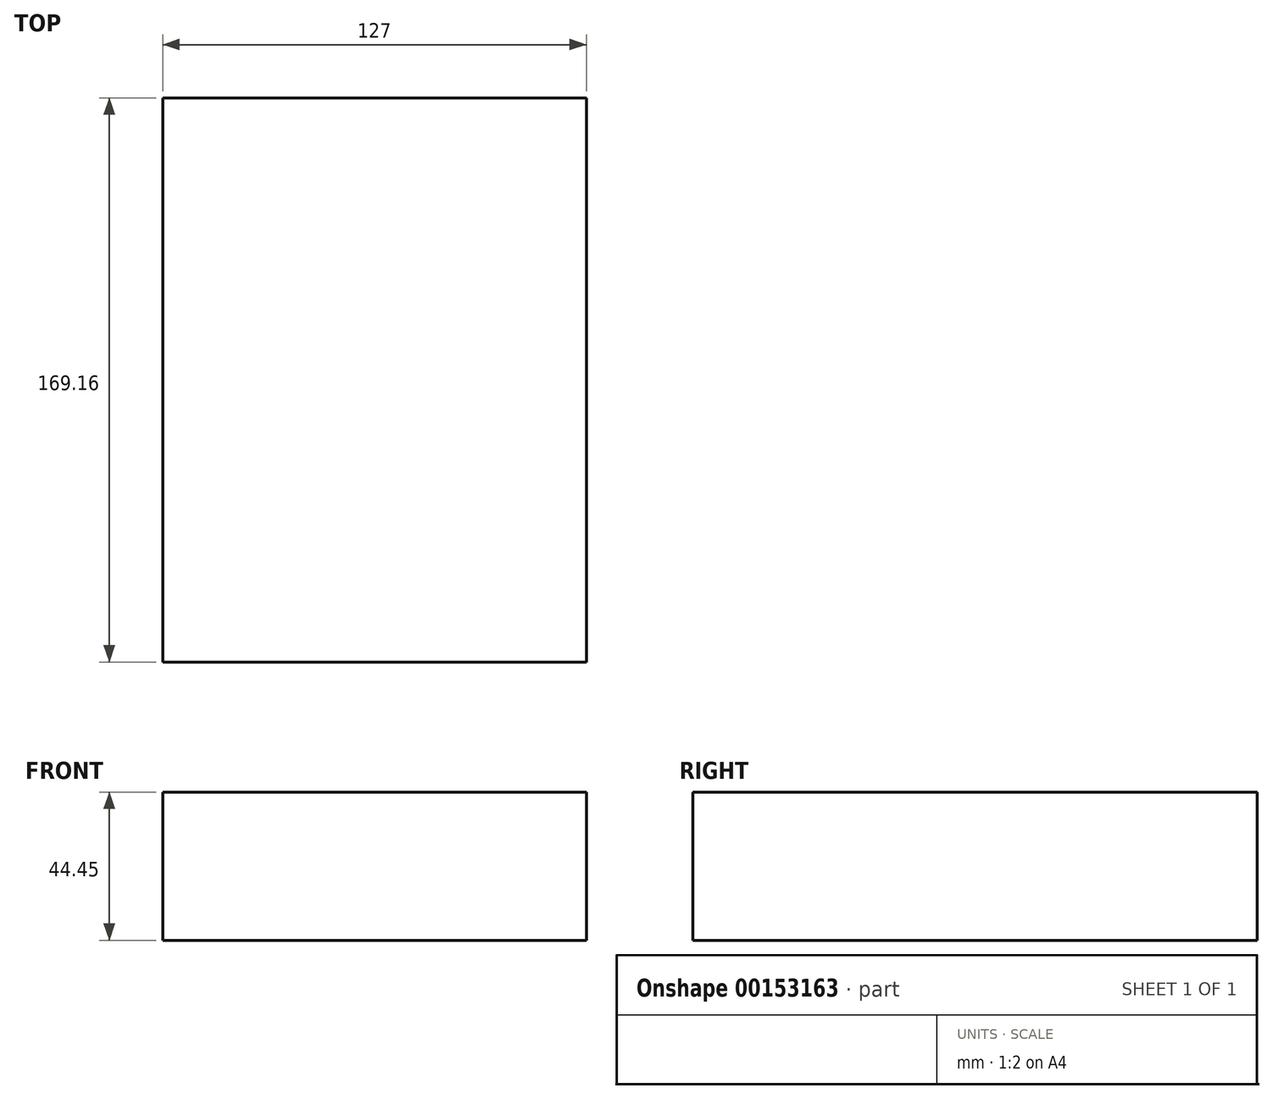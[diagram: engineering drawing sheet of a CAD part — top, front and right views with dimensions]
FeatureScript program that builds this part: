
annotation { "Feature Type Name" : "Feature", "Feature Type Description" : "" }
export const myFeature = defineFeature(function(context is Context, id is Id, definition is map)
    precondition{}
    {
        {
            var Q0;
            Q0=qCreatedBy(makeId("Top.planeOp"),FACE);
            var sketch = newSketch(context, id + "F0", { "sketchPlane" : qUnion([Q0])});
            skLineSegment(sketch, "E0.bottom", {"start": v(0, 0) * mm, "end": v(127, 0) * mm});
            skLineSegment(sketch, "E0.top", {"start": v(0, 169.16) * mm, "end": v(127, 169.16) * mm});
            skLineSegment(sketch, "E0.left", {"start": v(0, 0) * mm, "end": v(0, 169.16) * mm});
            skLineSegment(sketch, "E0.right", {"start": v(127, 0) * mm, "end": v(127, 169.16) * mm});
            skSolve(sketch);
        }
        {
            var Q0;
            Q0 = qSketchRegion(id + "F0", true);
            extrude(context, id + "F1", {"entities" : qUnion([Q0]), "depth" : 44.45 * mm});
        }
    });
